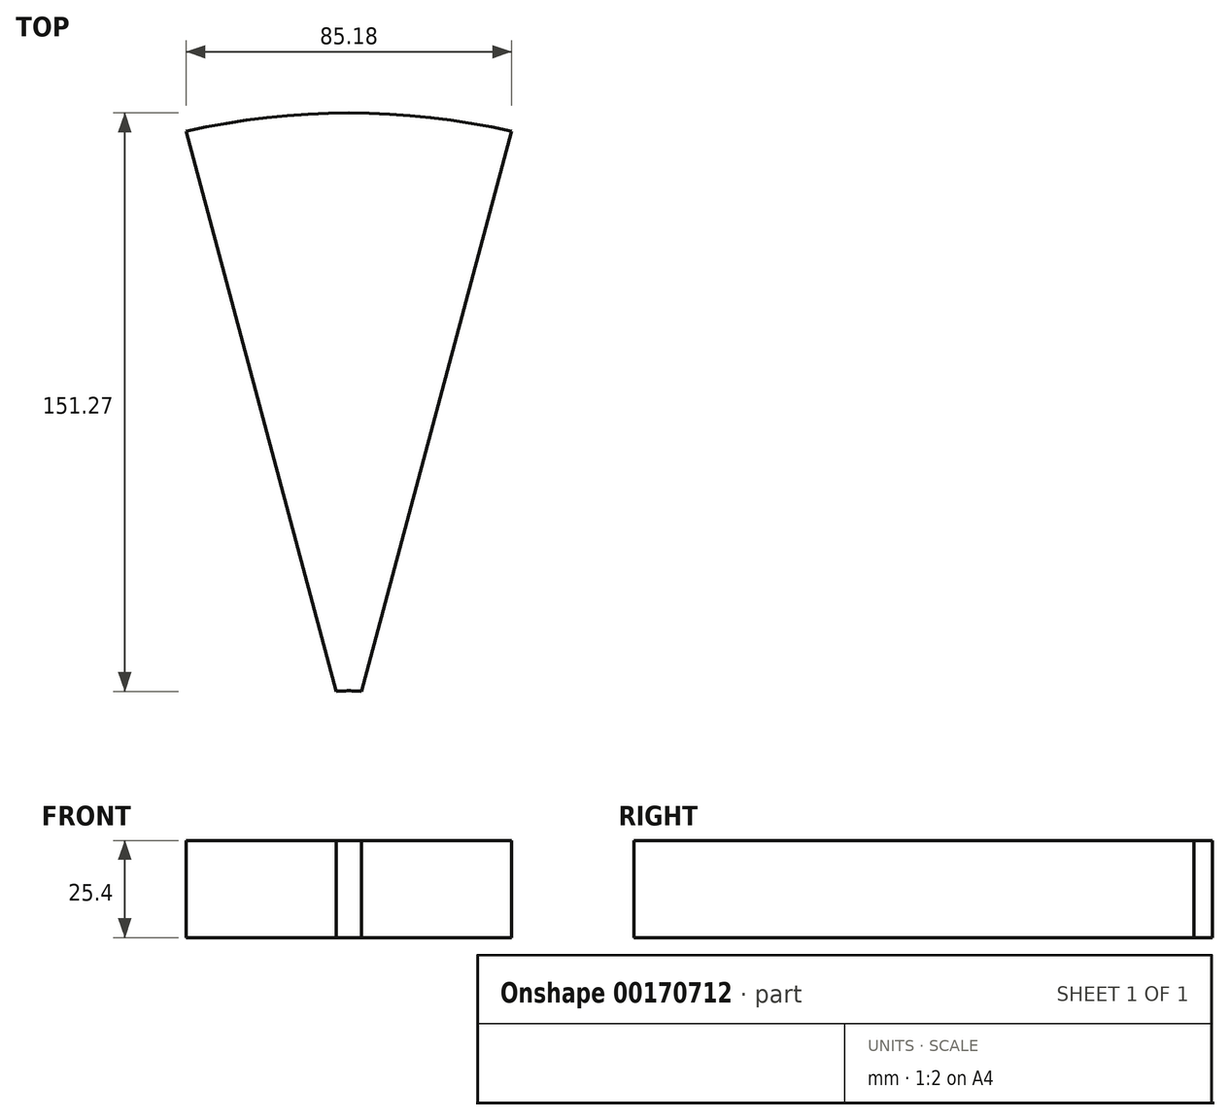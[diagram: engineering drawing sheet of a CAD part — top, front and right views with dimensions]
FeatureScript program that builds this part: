
annotation { "Feature Type Name" : "Feature", "Feature Type Description" : "" }
export const myFeature = defineFeature(function(context is Context, id is Id, definition is map)
    precondition{}
    {
        {
            var Q0;
            Q0=qCreatedBy(makeId("Top.planeOp"),FACE);
            var sketch = newSketch(context, id + "F0", { "sketchPlane" : qUnion([Q0])});
            skArc(sketch, "E0", {"start": v(50.4, 190.29) * mm, "mid": v(0, 196.85) * mm, "end": v(-50.4, 190.29) * mm, "construction": true});
            skArc(sketch, "E1", {"start": v(8, 32.04) * mm, "mid": v(0, 33.02) * mm, "end": v(-8, 32.04) * mm, "construction": true});
            skLineSegment(sketch, "E2", {"start": v(8, 32.04) * mm, "end": v(50.4, 190.29) * mm, "construction": true});
            skLineSegment(sketch, "E3", {"start": v(-50.4, 190.29) * mm, "end": v(-8, 32.04) * mm, "construction": true});
            skLineSegment(sketch, "E4", {"start": v(0, 0) * mm, "end": v(0, 184.5) * mm});
            skArc(sketch, "E5", {"start": v(42.6, 185.68) * mm, "mid": v(0, 190.5) * mm, "end": v(-42.6, 185.68) * mm});
            skLineSegment(sketch, "E6", {"start": v(3.35, 39.23) * mm, "end": v(42.6, 185.68) * mm});
            skLineSegment(sketch, "E7", {"start": v(-42.6, 185.68) * mm, "end": v(-3.35, 39.23) * mm});
            skArc(sketch, "E8", {"start": v(3.35, 39.23) * mm, "mid": v(0, 39.37) * mm, "end": v(-3.35, 39.23) * mm});
            skSolve(sketch);
        }
        {
            var Q0;
            Q0=qSketchRegion(id+"F0",true);
            extrude(context, id + "F1", {"entities" : qUnion([Q0]), "depth" : 25.4 * mm});
        }
    });
